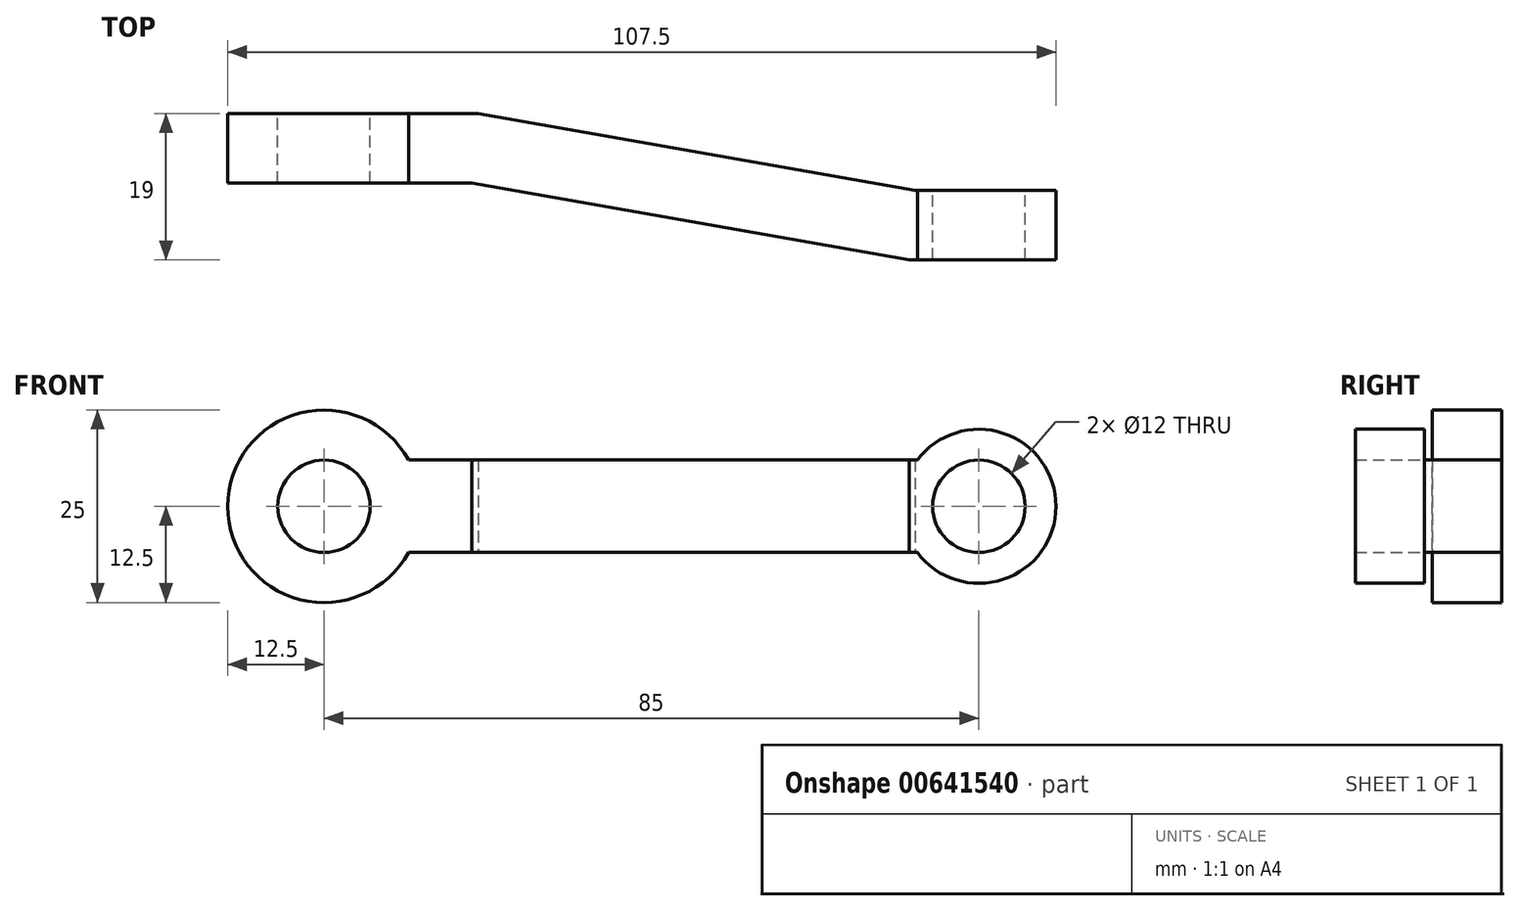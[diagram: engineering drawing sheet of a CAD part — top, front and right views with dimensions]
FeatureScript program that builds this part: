
annotation { "Feature Type Name" : "Feature", "Feature Type Description" : "" }
export const myFeature = defineFeature(function(context is Context, id is Id, definition is map)
    precondition{}
    {
        {
            var Q0;
            Q0=qCreatedBy(makeId("Front.planeOp"),FACE);
            var sketch = newSketch(context, id + "F0", { "sketchPlane" : qUnion([Q0])});
            skCircle(sketch, "E0", {"center": v(0, 0) * mm, "radius": 12.5 * mm});
            skCircle(sketch, "E1", {"center": v(85, 0) * mm, "radius": 10 * mm});
            skLineSegment(sketch, "E2", {"start": v(10.97, 6) * mm, "end": v(77, 6) * mm});
            skLineSegment(sketch, "E3", {"start": v(0, 0) * mm, "end": v(85, 0) * mm, "construction": true});
            skLineSegment(sketch, "E4.MirrorCS", {"start": v(10.97, -6) * mm, "end": v(77, -6) * mm});
            skCircle(sketch, "E5", {"center": v(0, 0) * mm, "radius": 6 * mm});
            skCircle(sketch, "E6", {"center": v(85, 0) * mm, "radius": 6 * mm});
            skSolve(sketch);
        }
        {
            var Q0;
            Q0 = qSketchRegion(id + "F0", true);
            extrude(context, id + "F1", {"entities" : qUnion([Q0]), "depth" : 25 * mm, "offsetDistance" : 25 * mm});
        }
        {
            var Q0;
            Q0=qCreatedBy(makeId("Top.planeOp"),FACE);
            var sketch = newSketch(context, id + "F2", { "sketchPlane" : qUnion([Q0])});
            skLineSegment(sketch, "E7", {"start": v(-12.5, 0) * mm, "end": v(20, 0) * mm});
            skLineSegment(sketch, "E8", {"start": v(20, 0) * mm, "end": v(76.7, -10) * mm});
            skLineSegment(sketch, "E9", {"start": v(76.7, -10) * mm, "end": v(95, -10) * mm});
            skLineSegment(sketch, "E10.0", {"start": v(75.92, -19) * mm, "end": v(95, -19) * mm});
            skLineSegment(sketch, "E10.1", {"start": v(19.21, -9) * mm, "end": v(75.92, -19) * mm});
            skLineSegment(sketch, "E10.2", {"start": v(-12.5, -9) * mm, "end": v(19.21, -9) * mm});
            skLineSegment(sketch, "E11", {"start": v(-12.5, -25) * mm, "end": v(-12.5, 0) * mm});
            skLineSegment(sketch, "E12", {"start": v(-12.5, -9) * mm, "end": v(-12.5, 0) * mm});
            skLineSegment(sketch, "E13", {"start": v(95, -19) * mm, "end": v(95, -10) * mm});
            skLineSegment(sketch, "E14", {"start": v(95, -2) * mm, "end": v(95, -25) * mm});
            skSolve(sketch);
        }
        {
            var Q0;
            Q0 = qSketchRegion(id + "F2", true);
            extrude(context, id + "F3", {"entities" : qUnion([Q0]), "operationType" : NewBodyOperationType.INTERSECT, "endBound" : BoundingType.SYMMETRIC, "depth" : 25 * mm, "offsetDistance" : 25 * mm});
        }
    });
